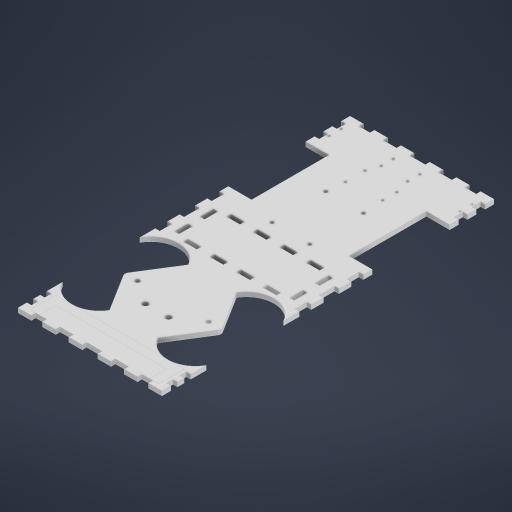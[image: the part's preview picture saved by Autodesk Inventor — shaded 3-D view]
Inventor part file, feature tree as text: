
AUTODESK INVENTOR PART (.ipt)
format: ipt  version: 2023.2 (Build 272271000, 271)  size: 607,744 bytes
history: native  units: mm
features: sketch x7, hole x3, other x1
ambient origin geometry x8: Origin, YZ Plane, XZ Plane, XY Plane, X Axis, Y Axis, Z Axis, Center Point
bodies: Body1 (feature_tree)
feature tree (11):
  hole  "Hole1"  [1 undecoded]
  hole  "Hole2"  [1 undecoded]
  hole  "Hole3"  [1 undecoded]
  other  "Mark1"
  sketch  "Sketch1"  dims[d122=130.0mm d123=300.0mm]
  sketch  "Sketch3"  dims[d128=75.0mm d158=33.0mm]
  sketch  "Sketch4"  dims[d159=6.108652mm d160=6.108652mm]
  sketch  "Sketch5"  dims[d161=4.0mm]
  sketch  "Sketch7"  dims[d169=6.108652mm d170=6.108652mm d172=75.0mm]
  sketch  "Sketch8"  dims[d175=33.0mm]
  sketch  "Sketch9"  dims[d179=33.0mm d181=4.0mm d182=0.0mm d183=70.0mm d186=35.0mm d187=21.0mm d188=75.0mm d189=70.0mm d190=21.0mm d191=75.0mm d196=3.0mm d201=34.0mm d202=48.5mm d205=75.0mm d208=3.0mm d209=5.0mm d210=3.0mm d211=6.0mm d212=4.0mm d213=2.0mm d214=90.0deg d215=8.0mm d216=20.594885mm d217=75.0mm d219=4.0mm d220=33.0mm d221=4.0mm d222=6.0mm d223=4.0mm d224=2.0mm d225=90.0deg d226=8.0mm d227=20.594885mm d228=21.0mm d229=5.0mm d231=21.0mm d233=14.5mm d234=5.0mm d235=6.0mm d236=4.0mm d237=2.0mm d238=90.0deg d239=8.0mm d240=20.594885mm d242=6.0mm d244=4.0mm d245=6.0mm d246=6.0mm d252=11.0mm d253=14.0mm d256=14.0mm d257=11.0mm d259=11.0mm d263=11.0mm d264=8.0mm d265=8.0mm d266=8.0mm d267=8.0mm d268=8.0mm d269=8.0mm d270=4.0mm d271=0.0mm d272=12.0mm d273=10.0mm d274=12.0mm d275=14.0mm d276=12.0mm d277=10.0mm d278=12.0mm d279=12.0mm d280=12.0mm d281=12.0mm d282=12.0mm d284=10.0mm d285=12.0mm d286=14.0mm d287=12.0mm d288=10.0mm d294=12.0mm d295=12.0mm d296=12.0mm d297=12.0mm d298=12.0mm d299=12.0mm d300=14.0mm d301=8.0mm d308=116.0mm d309=8.0mm d310=8.0mm d311=23.031521mm d313=35.0mm d316=12.0mm d318=12.0mm d319=100.0mm d320=4.0mm d321=12.0mm d323=8.0mm d324=12.0mm d326=16.0mm d327=4.0mm d328=0.0mm d329=2.0mm d330=15.0mm d333=2.0mm d334=11.0mm d335=4.0mm d336=0.0mm d339=47.0mm d341=2.0mm d342=17.65mm d346=2.5mm d347=2.5mm d348=31.2mm d349=32.0mm d350=4.0mm d351=0.0mm d9=0.5mm d10=0.872665mm d11=0.5mm d12=0.872665mm d13=0.5mm d14=0.872665mm d27=0.5mm d28=0.872665mm d29=0.5mm d30=0.872665mm d88=0.5mm d89=0.872665mm d90=0.5mm d91=0.872665mm d116=0.5mm d117=0.872665mm d118=0.5mm d119=0.872665mm d154=0.5mm d155=0.872665mm d156=0.5mm d157=0.872665mm d184=0.872665mm]
note: 3 required parameter values undecoded (feature->parameter linkage not recoverable at this tier; creation-order binding heuristic only, values carry confidence <= 0.55)
